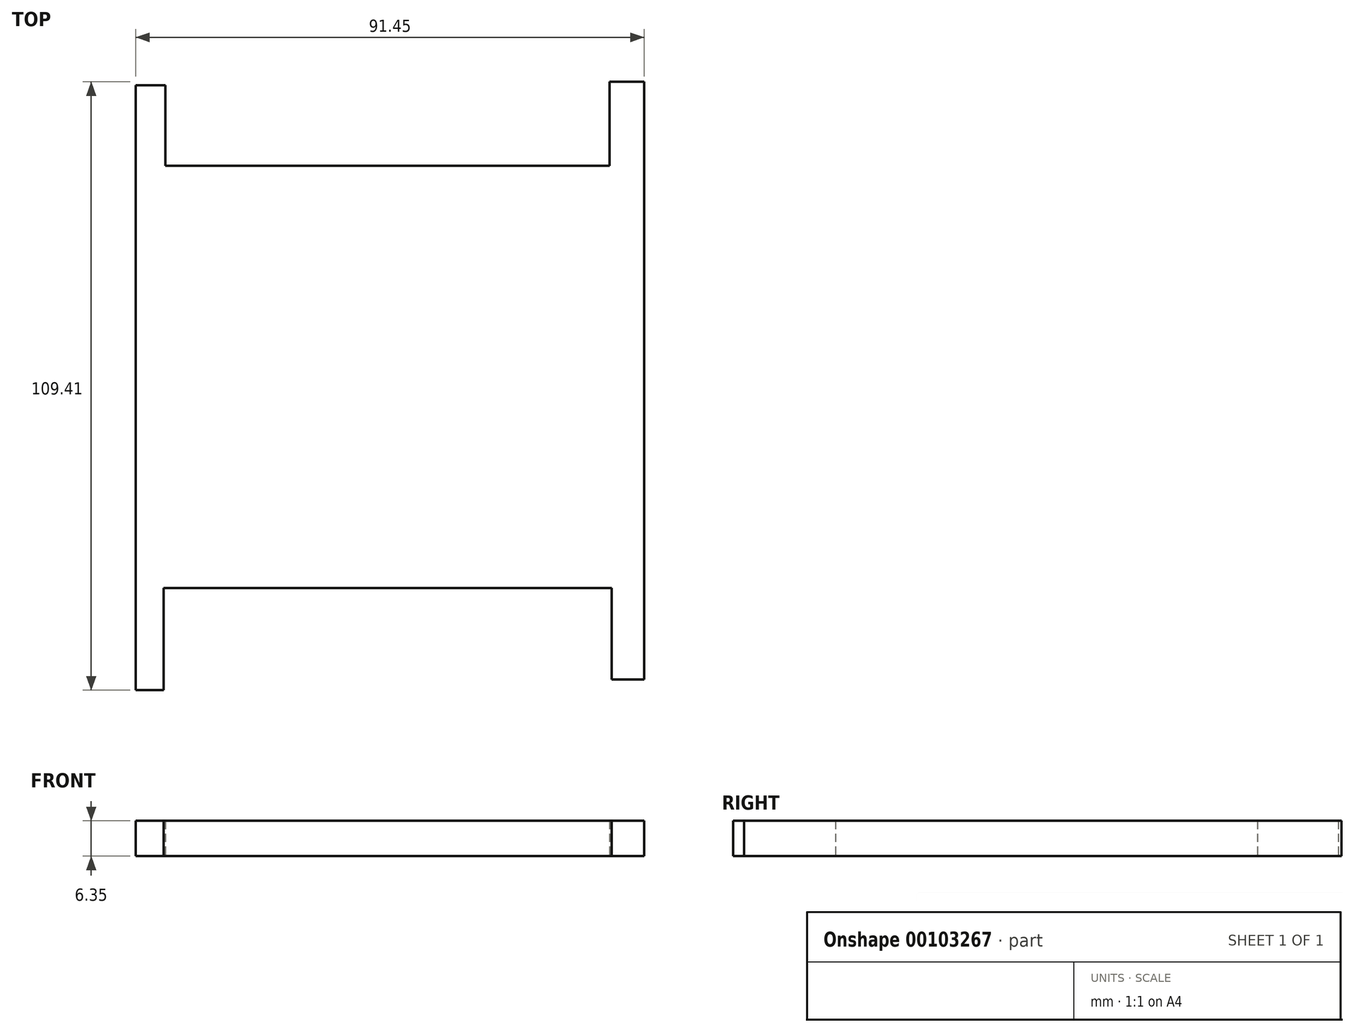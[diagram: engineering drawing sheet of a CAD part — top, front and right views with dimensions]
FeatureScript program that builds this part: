
annotation { "Feature Type Name" : "Feature", "Feature Type Description" : "" }
export const myFeature = defineFeature(function(context is Context, id is Id, definition is map)
    precondition{}
    {
        {
            var Q0;
            Q0=qCreatedBy(makeId("Top.planeOp"),FACE);
            var sketch = newSketch(context, id + "F0", { "sketchPlane" : qUnion([Q0])});
            skLineSegment(sketch, "E0.bottom", {"start": v(27.02, -34.11) * mm, "end": v(-64.43, -34.11) * mm});
            skLineSegment(sketch, "E0.top", {"start": v(27.02, 41.81) * mm, "end": v(-64.43, 41.81) * mm});
            skLineSegment(sketch, "E0.left", {"start": v(27.02, -34.11) * mm, "end": v(27.02, 41.81) * mm});
            skLineSegment(sketch, "E0.right", {"start": v(-64.43, -34.11) * mm, "end": v(-64.43, 41.81) * mm});
            skLineSegment(sketch, "E1.bottom", {"start": v(-64.43, 41.81) * mm, "end": v(-59.1, 41.81) * mm});
            skLineSegment(sketch, "E1.top", {"start": v(-64.43, 56.31) * mm, "end": v(-59.1, 56.31) * mm});
            skLineSegment(sketch, "E1.left", {"start": v(-64.43, 41.81) * mm, "end": v(-64.43, 56.31) * mm});
            skLineSegment(sketch, "E1.right", {"start": v(-59.1, 41.81) * mm, "end": v(-59.1, 56.31) * mm});
            skLineSegment(sketch, "E2.bottom", {"start": v(27.02, 41.81) * mm, "end": v(20.77, 41.81) * mm});
            skLineSegment(sketch, "E2.top", {"start": v(27.02, 56.9) * mm, "end": v(20.77, 56.9) * mm});
            skLineSegment(sketch, "E2.left", {"start": v(27.02, 41.81) * mm, "end": v(27.02, 56.9) * mm});
            skLineSegment(sketch, "E2.right", {"start": v(20.77, 41.81) * mm, "end": v(20.77, 56.9) * mm});
            skLineSegment(sketch, "E3.bottom", {"start": v(-64.43, -34.11) * mm, "end": v(-59.39, -34.11) * mm});
            skLineSegment(sketch, "E3.top", {"start": v(-64.43, -52.51) * mm, "end": v(-59.39, -52.51) * mm});
            skLineSegment(sketch, "E3.left", {"start": v(-64.43, -34.11) * mm, "end": v(-64.43, -52.51) * mm});
            skLineSegment(sketch, "E3.right", {"start": v(-59.39, -34.11) * mm, "end": v(-59.39, -52.51) * mm});
            skLineSegment(sketch, "E4.bottom", {"start": v(27.02, -34.11) * mm, "end": v(21.15, -34.11) * mm});
            skLineSegment(sketch, "E4.top", {"start": v(27.02, -50.56) * mm, "end": v(21.15, -50.56) * mm});
            skLineSegment(sketch, "E4.left", {"start": v(27.02, -34.11) * mm, "end": v(27.02, -50.56) * mm});
            skLineSegment(sketch, "E4.right", {"start": v(21.15, -34.11) * mm, "end": v(21.15, -50.56) * mm});
            skSolve(sketch);
        }
        {
            var Q0;
            Q0 = qSketchRegion(id + "F0", true);
            extrude(context, id + "F1", {"entities" : qUnion([Q0]), "depth" : 6.35 * mm});
        }
    });
